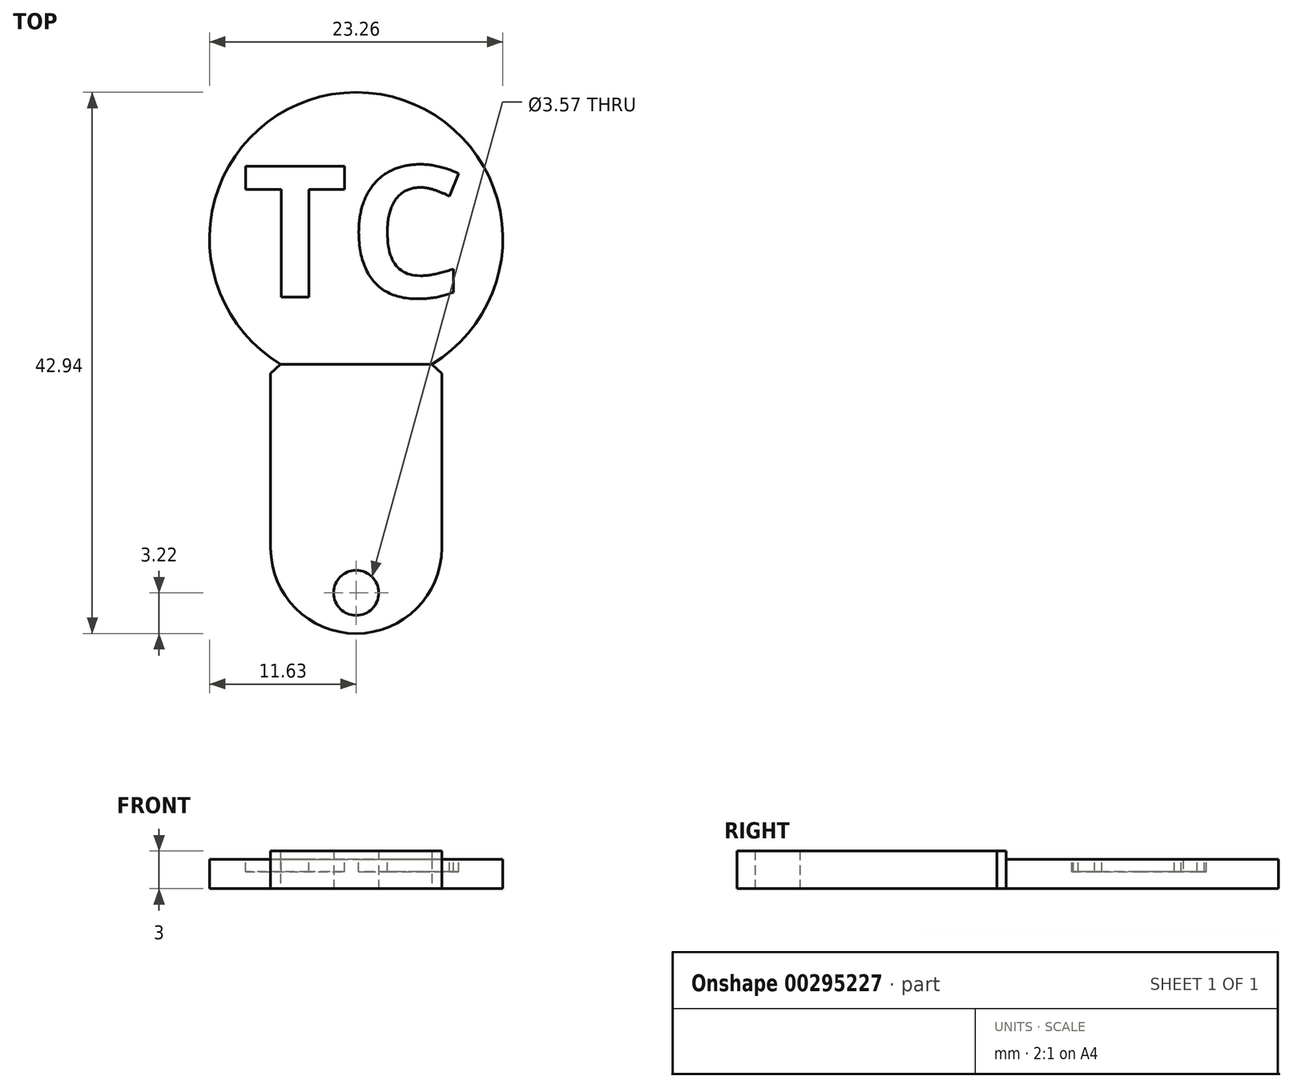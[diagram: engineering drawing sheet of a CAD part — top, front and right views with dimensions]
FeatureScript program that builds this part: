
annotation { "Feature Type Name" : "Feature", "Feature Type Description" : "" }
export const myFeature = defineFeature(function(context is Context, id is Id, definition is map)
    precondition{}
    {
        {
            var Q0;
            Q0=qCreatedBy(makeId("Top.planeOp"),FACE);
            var sketch = newSketch(context, id + "F0", { "sketchPlane" : qUnion([Q0])});
            skCircle(sketch, "E0", {"center": v(0, 0) * mm, "radius": 11.62 * mm});
            skLineSegment(sketch, "E1", {"start": v(-6, -9.96) * mm, "end": v(6, -9.96) * mm});
            skSolve(sketch);
        }
        {
            var Q0;
            {var subQ0=sQuery(id+"F0.wireOp",EDGE,"E1");Q0=makeQuery(id+"F0.imprint","IMPRINT",FACE,{"disambiguationData":[TD([[makeQuery(id+"F0.imprint","IMPRINT",EDGE,{"derivedFrom":subQ0}),1.0]])]});}
            extrude(context, id + "F1", {"entities" : qUnion([Q0]), "depth" : 2.33 * mm});
        }
        {
            var Q0;
            Q0=qCreatedBy(makeId("Top.planeOp"),FACE);
            var sketch = newSketch(context, id + "F2", { "sketchPlane" : qUnion([Q0])});
            skLineSegment(sketch, "E2.0", {"start": v(-6, -9.96) * mm, "end": v(6, -9.96) * mm});
            skPoint(sketch, "E3.0", {"position": v(0, 0) * mm});
            skLineSegment(sketch, "E4", {"start": v(0, 0) * mm, "end": v(0, -24.53) * mm, "construction": true});
            skLineSegment(sketch, "E5", {"start": v(0, -24.53) * mm, "end": v(6.78, -24.53) * mm, "construction": true});
            skLineSegment(sketch, "E6", {"start": v(6.78, -24.53) * mm, "end": v(6.78, -10.7) * mm});
            skLineSegment(sketch, "E7", {"start": v(6.78, -10.7) * mm, "end": v(6, -9.96) * mm});
            skArc(sketch, "E8", {"start": v(-6.78, -24.53) * mm, "mid": v(0, -31.31) * mm, "end": v(6.78, -24.53) * mm});
            skLineSegment(sketch, "E9.MirrorCS", {"start": v(-6.78, -24.53) * mm, "end": v(-6.78, -10.7) * mm});
            skLineSegment(sketch, "E10.MirrorCS", {"start": v(-6.78, -10.7) * mm, "end": v(-6, -9.96) * mm});
            skCircle(sketch, "E11", {"center": v(0, -28.1) * mm, "radius": 1.79 * mm});
            skSolve(sketch);
        }
        {
            var Q0;
            Q0=makeQuery(id+"F2.imprint","IMPRINT",FACE,{"disambiguationData":[TD([[makeQuery(id+"F2.imprint","IMPRINT",EDGE,{"derivedFrom":sQuery(id+"F2.wireOp",EDGE,"E2.0")}),-1.0]])]});
            extrude(context, id + "F3", {"entities" : qUnion([Q0]), "operationType" : NewBodyOperationType.ADD, "depth" : 3 * mm});
        }
        {
            var Q0;
            Q0=makeQuery(id+"F1.opExtrude","CAP_FACE",FACE,{"disambiguationData":[OSD([sQuery(id+"F0.wireOp",EDGE,"E0"),sQuery(id+"F0.wireOp",EDGE,"E1")])],"isStart":false});
            var sketch = newSketch(context, id + "F4", { "sketchPlane" : qUnion([Q0])});
            skText(sketch, "E12", { "text": "TC", "fontName": "OpenSans-Bold.ttf"});
            const initialGuessF4  = {"E12": [-0.00906, -0.00462, 1, 0, 0.01047]};
            skSetInitialGuess(sketch, initialGuessF4);
            skSolve(sketch);
        }
        {
            var Q0;
            Q0=makeQuery(id+"F4.imprint","IMPRINT",FACE,{"disambiguationData":[TD([[makeQuery(id+"F4.imprint","IMPRINT",EDGE,{"derivedFrom":sQuery(id+"F4.wireOp",EDGE,"E12.sketch_text.stroke-8")}),-1.0]])]});
            var Q1;
            Q1=makeQuery(id+"F4.imprint","IMPRINT",FACE,{"disambiguationData":[TD([[makeQuery(id+"F4.imprint","IMPRINT",EDGE,{"derivedFrom":sQuery(id+"F4.wireOp",EDGE,"E12.sketch_text.stroke-0")}),-1.0]])]});
            extrude(context, id + "F5", {"entities" : qUnion([Q0, Q1]), "operationType" : NewBodyOperationType.REMOVE, "oppositeDirection" : true, "depth" : 1 * mm});
        }
    });
